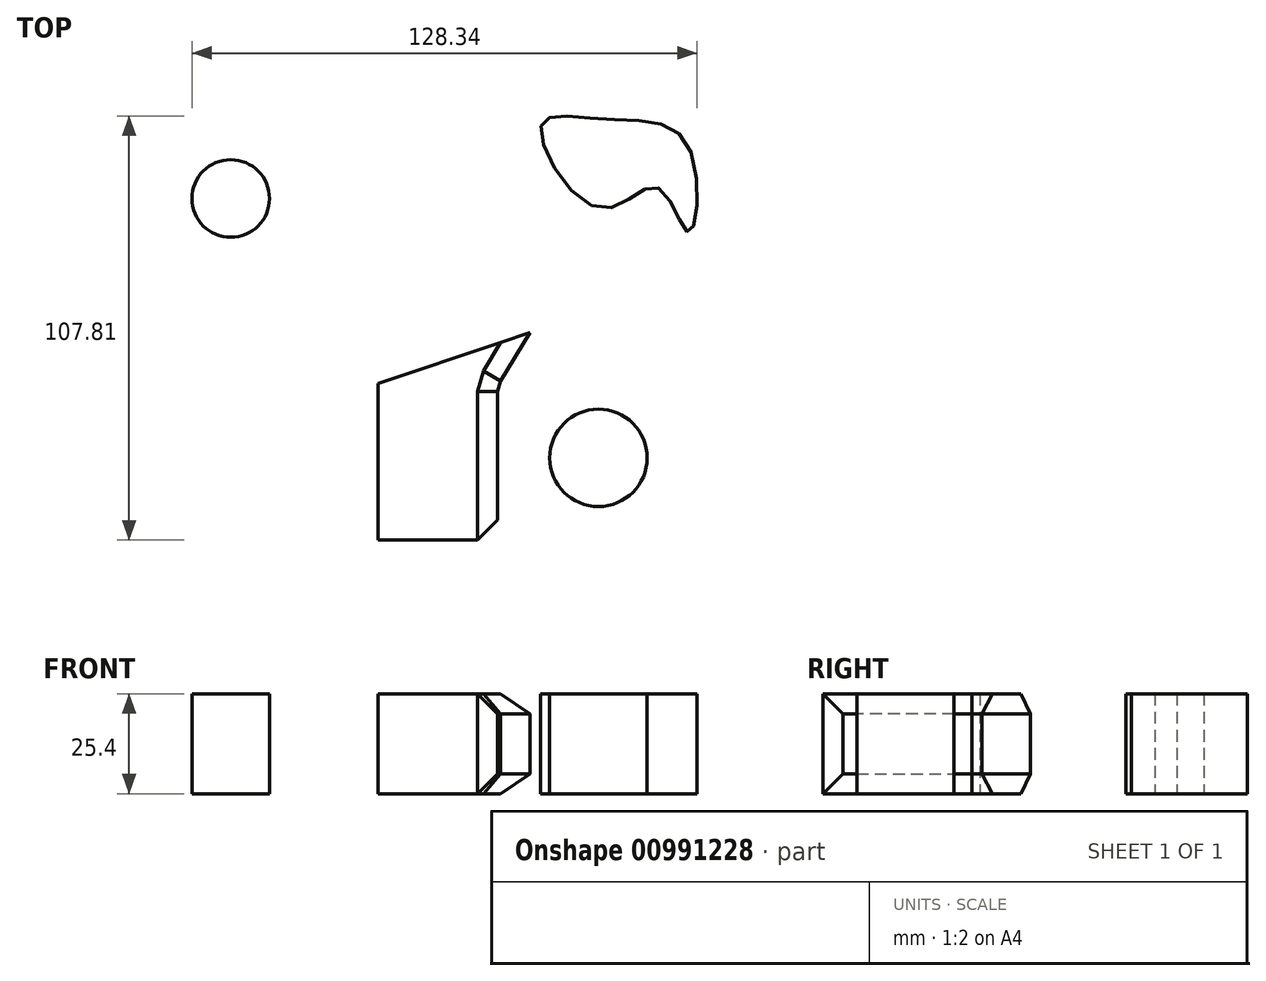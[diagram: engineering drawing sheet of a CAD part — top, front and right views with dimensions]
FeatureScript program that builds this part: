
annotation { "Feature Type Name" : "Feature", "Feature Type Description" : "" }
export const myFeature = defineFeature(function(context is Context, id is Id, definition is map)
    precondition{}
    {
        {
            var Q0;
            Q0=qCreatedBy(makeId("Top.planeOp"),FACE);
            var sketch = newSketch(context, id + "F0", { "sketchPlane" : qUnion([Q0])});
            skCircle(sketch, "E0", {"center": v(-55.35, 34.1) * mm, "radius": 16.6 * mm});
            skCircle(sketch, "E1", {"center": v(-55.35, 34.1) * mm, "radius": 9.85 * mm});
            skSolve(sketch);
        }
        {
            var Q0;
            Q0=makeQuery(id+"F0.imprint","IMPRINT",FACE,{"disambiguationData":[TD([[makeQuery(id+"F0.imprint","IMPRINT",EDGE,{"derivedFrom":sQuery(id+"F0.wireOp",EDGE,"E1")}),1.0]])]});
            extrude(context, id + "F1", {"entities" : qUnion([Q0]), "depth" : 25.4 * mm, "offsetDistance" : 25.4 * mm});
        }
        {
            var Q0;
            Q0=qCreatedBy(makeId("Top.planeOp"),FACE);
            var sketch = newSketch(context, id + "F2", { "sketchPlane" : qUnion([Q0])});
            skLineSegment(sketch, "E2", {"start": v(22.94, 19.03) * mm, "end": v(28.71, 46.87) * mm});
            skLineSegment(sketch, "E3", {"start": v(28.71, 46.87) * mm, "end": v(62.95, 24.18) * mm});
            skLineSegment(sketch, "E4", {"start": v(62.95, 24.18) * mm, "end": v(22.94, 19.03) * mm});
            skLineSegment(sketch, "E5", {"start": v(-17.89, -12.93) * mm, "end": v(-17.89, -52.73) * mm});
            skLineSegment(sketch, "E6", {"start": v(-17.89, -52.73) * mm, "end": v(12.42, -52.73) * mm});
            skLineSegment(sketch, "E7", {"start": v(12.42, -52.73) * mm, "end": v(12.42, -13.55) * mm});
            skLineSegment(sketch, "E8", {"start": v(-17.89, -12.93) * mm, "end": v(20.67, 0) * mm});
            skLineSegment(sketch, "E9", {"start": v(20.67, 0) * mm, "end": v(12.42, -13.55) * mm});
            skSolve(sketch);
        }
        {
            var Q0;
            Q0=makeQuery(id+"F2.imprint","IMPRINT",FACE,{"disambiguationData":[TD([[makeQuery(id+"F2.imprint","IMPRINT",EDGE,{"derivedFrom":sQuery(id+"F2.wireOp",EDGE,"E5")}),1.0]])]});
            extrude(context, id + "F3", {"entities" : qUnion([Q0]), "depth" : 25.4 * mm, "offsetDistance" : 25.4 * mm});
        }
        {
            var Q0;
            Q0=qCreatedBy(makeId("Top.planeOp"),FACE);
            var sketch = newSketch(context, id + "F4", { "sketchPlane" : qUnion([Q0])});
            skFitSpline(sketch, "E10", {"points": [v(23.48, 52.49) * mm, v(38.84, 31.55) * mm, v(53.15, 36.9) * mm, v(60.94, 25.62) * mm, v(60.7, 47.75) * mm, v(38.74, 54.3) * mm, v(23.48, 52.49) * mm]});
            skSolve(sketch);
        }
        {
            var Q0;
            Q0=makeQuery(id+"F4.imprint","IMPRINT",FACE,{"disambiguationData":[TD([[makeQuery(id+"F4.imprint","IMPRINT",EDGE,{"derivedFrom":sQuery(id+"F4.wireOp",EDGE,"E10")}),1.0]])]});
            extrude(context, id + "F5", {"entities" : qUnion([Q0]), "depth" : 25.4 * mm, "offsetDistance" : 25.4 * mm});
        }
        {
            var Q0;
            Q0=makeQuery(id+"F3.opExtrude","CAP_EDGE",EDGE,{"disambiguationData":[OSD([sQuery(id+"F2.wireOp",EDGE,"E7")])],"isStart":false});
            var Q1;
            Q1=makeQuery(id+"F3.opExtrude","SWEPT_FACE",FACE,{"disambiguationData":[OSD([sQuery(id+"F2.wireOp",EDGE,"E7")])]});
            chamfer(context, id + "F6", {"entities" : qUnion([Q0, Q1]), "width" : 5.08 * mm, "tangentPropagation" : true});
        }
        {
            var Q0;
            Q0=qCreatedBy(makeId("Top.planeOp"),FACE);
            var sketch = newSketch(context, id + "F7", { "sketchPlane" : qUnion([Q0])});
            skCircle(sketch, "E11", {"center": v(38.05, -31.8) * mm, "radius": 12.37 * mm});
            skSolve(sketch);
        }
        {
            var Q0;
            Q0=makeQuery(id+"F7.imprint","IMPRINT",FACE,{"disambiguationData":[TD([[makeQuery(id+"F7.imprint","IMPRINT",EDGE,{"derivedFrom":sQuery(id+"F7.wireOp",EDGE,"E11")}),1.0]])]});
            extrude(context, id + "F8", {"entities" : qUnion([Q0]), "depth" : 25.4 * mm, "offsetDistance" : 25.4 * mm});
        }
    });
